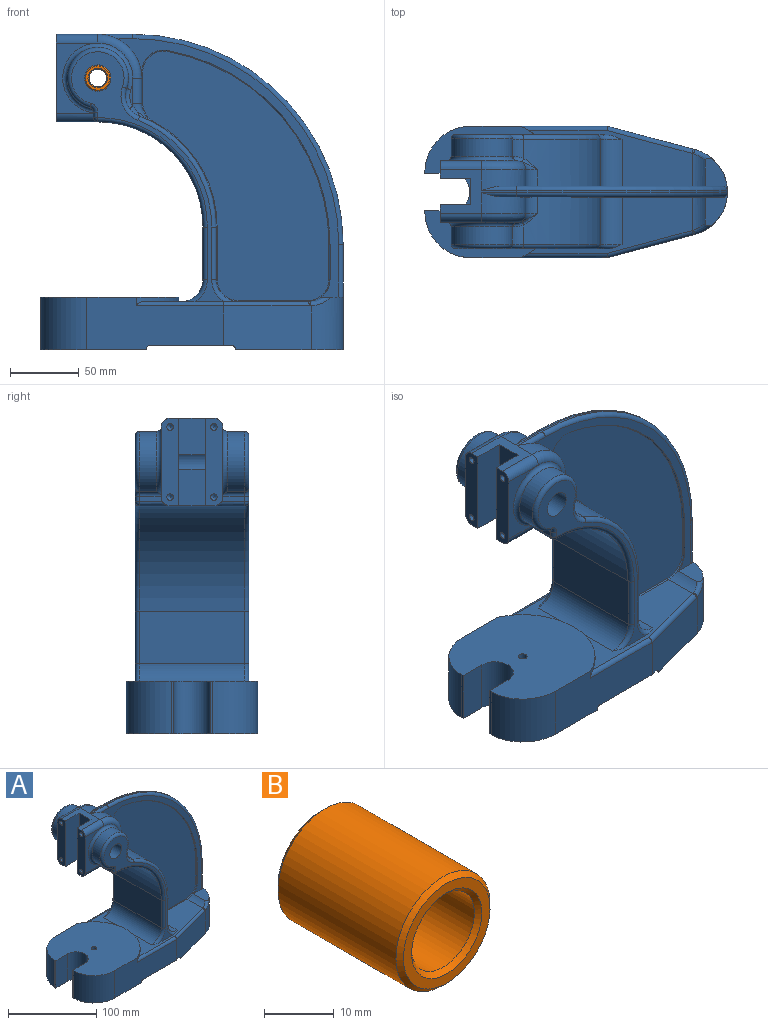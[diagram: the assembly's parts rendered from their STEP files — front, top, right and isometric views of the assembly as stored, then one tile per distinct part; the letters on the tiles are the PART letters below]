
ASSEMBLY  parts=2 mates=1
PART A: 180 faces, bbox 234.5x98.1x244 mm
  f0: plane 63.5x12.7mm, normal (-1,0,0), area 753.5mm2, adj f2,f15,f17,f92,f97,f149,f151,f158
  f1: plane 20.23x2.34mm, normal (0,1,0), area 23.9mm2, adj f90,f91,f104,f106
  f2: plane 50.8x30.1mm, normal (0,-1,0), area 515.4mm2, adj f0,f83,f92,f97,f124
  f3: plane 22.59x12.73mm, normal (1,0,0), area 235.4mm2, adj f19,f26,f32,f87,f94,f174
  f4: plane 22.59x12.73mm, normal (1,0,0), area 235.4mm2, adj f10,f14,f33,f86,f90,f164
  f5: plane 99.19x38.1mm, normal (0,-1,0), area 3202mm2, adj f6,f40,f46,f49,f52,f58,f76,f133
  f6: plane 100x95.25mm, normal (0,0,1), area 7398mm2, adj f5,f43,f44,f48,f54,f55,f56,f57
  f7: plane 38.1x34.96mm, normal (1,0,0), area 1331.9mm2, adj f8,f9,f114,f169
  f8: cylinder r=15.88mm len=34.96mm, axis (0,1,0), area 871.7mm2, adj f7,f37,f115,f167
  f9: cylinder r=85.72mm len=80.21mm, axis (0,1,0), area 3442.3mm2, adj f7,f80,f86,f100,f113,f168
  f10: cylinder r=15.88mm len=18.65mm, axis (0,1,0), area 22.7mm2, adj f4,f11,f33,f162
  f11: cylinder r=142.88mm len=140.67mm, axis (0,1,0), area 163.3mm2, adj f10,f12,f33,f160
  f12: plane 25.4x0.82mm, normal (-1,0,0), area 20.8mm2, adj f11,f13,f33,f161
  f13: cylinder r=15.88mm len=24.81mm, axis (0,1,0), area 242.1mm2, adj f12,f33,f37,f45,f139,f140,f163
  f14: cylinder r=31.75mm len=31.75mm, axis (0,1,0), area 616.8mm2, adj f4,f15,f33,f89,f141
  f15: plane 55.5x31.75mm, normal (0,0,1), area 573.2mm2, adj f0,f14,f16,f19,f31,f88,f92,f141
  f16: plane 63.5x12.7mm, normal (-1,0,0), area 753.5mm2, adj f15,f17,f21,f88,f96,f147,f153,f157
  f17: plane 31.75x30.1mm, normal (0,0,-1), area 533.2mm2, adj f0,f16,f18,f96,f97,f156,f157,f158
  f18: cylinder r=76.2mm len=76.2mm, axis (0,1,0), area 9120.7mm2, adj f17,f22,f103,f105,f119,f121
  f19: cylinder r=31.75mm len=31.75mm, axis (0,1,0), area 616.8mm2, adj f3,f15,f32,f93,f144
  f20: plane 20.23x2.34mm, normal (0,-1,0), area 23.9mm2, adj f94,f95,f122,f124
  f21: plane 50.8x30.1mm, normal (0,1,0), area 515.4mm2, adj f16,f78,f88,f96,f106
  f22: plane 76.2x38.1mm, normal (-1,0,0), area 2903.2mm2, adj f18,f98,f101,f117
  f23: cylinder r=15.88mm len=34.96mm, axis (0,1,0), area 871.7mm2, adj f24,f37,f132,f177
  f24: plane 38.1x34.96mm, normal (1,0,0), area 1331.9mm2, adj f23,f25,f131,f179
  f25: cylinder r=85.72mm len=80.21mm, axis (0,1,0), area 3442.3mm2, adj f24,f81,f87,f118,f130,f178
  f26: cylinder r=15.88mm len=18.65mm, axis (0,1,0), area 22.7mm2, adj f3,f27,f32,f172
  f27: cylinder r=142.88mm len=140.67mm, axis (0,1,0), area 163.3mm2, adj f26,f28,f32,f170
  f28: plane 25.4x0.82mm, normal (-1,0,0), area 20.8mm2, adj f27,f29,f32,f171
  f29: cylinder r=15.88mm len=24.81mm, axis (0,1,0), area 242.1mm2, adj f28,f32,f36,f37,f135,f136,f173
  f30: plane 76.2x7.92mm, normal (1,0,0), area 361.9mm2, adj f31,f36,f42,f45,f51,f53,f143,f146
  f31: cylinder r=152.4mm len=152.4mm, axis (0,1,0), area 377mm2, adj f15,f30,f142,f145
  f32: plane 187.33x160.79mm, normal (0,-1,0), area 1900.4mm2, adj f3,f19,f26,f27,f28,f29,f36,f144
  f33: plane 187.33x160.79mm, normal (0,1,0), area 1900.4mm2, adj f4,f10,f11,f12,f13,f14,f45,f141
  f34: plane 180.67x135mm, normal (0,-1,0), area 14138.8mm2, adj f170,f171,f172,f173,f174,f175,f176,f177
  f35: plane 180.67x135mm, normal (0,1,0), area 14138.8mm2, adj f160,f161,f162,f163,f164,f165,f166,f167
  f36: plane 26.58x18.73mm, normal (0,0,1), area 245.8mm2, adj f29,f30,f32,f53,f136,f146
  f37: plane 119.12x89.67mm, normal (0,0,1), area 4280.2mm2, adj f8,f13,f23,f29,f76,f77,f84,f98
  f38: cylinder r=3.17mm len=9.06mm, axis (0,1,0), area 40.9mm2, adj f40,f42,f52,f69
  f39: cylinder r=3.17mm len=7.93mm, axis (0,1,0), area 39.5mm2, adj f41,f46,f48,f65
  f40: plane 58.73x9.7mm, normal (0,0,-1), area 467.1mm2, adj f5,f38,f49,f52,f64,f69
  f41: plane 58.73x9.7mm, normal (0,0,-1), area 467.1mm2, adj f39,f47,f48,f50,f65,f67
  f42: plane 90.55x77.8mm, normal (0,0,-1), area 1454mm2, adj f30,f38,f47,f50,f51,f52,f53,f59
  f43: plane 38.1x1.61mm, normal (-1,0,0), area 61.5mm2, adj f6,f46,f54,f58
  f44: plane 38.1x1.61mm, normal (-1,0,0), area 61.5mm2, adj f6,f46,f55,f57
  f45: plane 26.58x18.73mm, normal (0,0,1), area 245.8mm2, adj f13,f30,f33,f51,f140,f143
  f46: plane 95.25x76.2mm, normal (0,0,-1), area 2029.8mm2, adj f5,f39,f43,f44,f48,f49,f54,f55
  f47: cylinder r=3.17mm len=9.06mm, axis (0,1,0), area 40.9mm2, adj f41,f42,f50,f67
  f48: plane 99.19x38.1mm, normal (0,1,0), area 3202mm2, adj f6,f39,f41,f46,f50,f57,f76,f137
  f49: cylinder r=3.17mm len=7.93mm, axis (0,1,0), area 39.5mm2, adj f5,f40,f46,f64
  f50: plane 63.64x32.15mm, normal (0.26,0.97,0), area 2053.6mm2, adj f41,f42,f47,f48,f51,f138,f139
  f51: cylinder r=31.75mm len=38.1mm, axis (0,0,-1), area 1379.2mm2, adj f30,f42,f45,f50,f140
  f52: plane 63.64x32.15mm, normal (0.26,-0.97,0), area 2053.6mm2, adj f5,f38,f40,f42,f53,f134,f135
  f53: cylinder r=31.75mm len=38.1mm, axis (0,0,-1), area 1379.2mm2, adj f30,f36,f42,f52,f136
  f54: plane 38.1x19.05mm, normal (0,1,0), area 725.8mm2, adj f6,f43,f46,f56
  f55: plane 38.1x19.05mm, normal (0,-1,0), area 725.8mm2, adj f6,f44,f46,f56
  f56: cylinder r=13.49mm len=38.1mm, axis (0,0,-1), area 1615.1mm2, adj f6,f46,f54,f55
  f57: cylinder r=33.32mm len=38.1mm, axis (0,0,-1), area 1963.7mm2, adj f6,f44,f46,f48
  f58: cylinder r=33.32mm len=38.1mm, axis (0,0,-1), area 1963.7mm2, adj f5,f6,f43,f46
  f59: plane 30.18x6.86mm, normal (-1,0,0), area 207mm2, adj f42,f60,f68,f70
  f60: plane 31.27x5.6mm, normal (0,0,-1), area 124.1mm2, adj f59,f61,f68,f70
  f61: cylinder r=23.8mm len=46.06mm, axis (0,1,0), area 499.2mm2, adj f60,f62,f67,f68,f69,f70
  f62: plane 84.13x79.4mm, normal (0,0,-1), area 5642.5mm2, adj f61,f64,f65,f66,f67,f69
  f63: plane 100.62x79.4mm, normal (0,0,-1), area 6568.5mm2, adj f64,f65,f66,f71,f72,f73,f74,f75
  f64: plane 98.15x30.18mm, normal (0,1,0), area 2718.8mm2, adj f40,f46,f49,f62,f63,f66,f69,f75
  f65: plane 98.15x30.18mm, normal (0,-1,0), area 2718.8mm2, adj f39,f41,f46,f62,f63,f66,f67,f74
  f66: plane 79.4x3.18mm, normal (-1,0,0), area 252.1mm2, adj f62,f63,f64,f65
  f67: plane 62.63x27.36mm, normal (-0.26,-0.97,0), area 1710.8mm2, adj f41,f42,f47,f61,f62,f65,f68
  f68: cylinder r=23.83mm len=30.18mm, axis (0,0,-1), area 814.8mm2, adj f42,f59,f60,f61,f67
  f69: plane 62.63x27.36mm, normal (-0.26,0.97,0), area 1710.8mm2, adj f38,f40,f42,f61,f62,f64,f70
  f70: cylinder r=23.83mm len=30.18mm, axis (0,0,-1), area 814.8mm2, adj f42,f59,f60,f61,f69
  f71: plane 30.18x10.12mm, normal (0,-1,0), area 305.3mm2, adj f46,f63,f73,f75
  f72: plane 30.18x10.12mm, normal (0,1,0), area 305.3mm2, adj f46,f63,f73,f74
  f73: cylinder r=21.42mm len=42.84mm, axis (0,0,-1), area 2030.4mm2, adj f46,f63,f71,f72
  f74: cylinder r=25.4mm len=30.18mm, axis (0,0,-1), area 986.2mm2, adj f46,f63,f65,f72
  f75: cylinder r=25.4mm len=30.18mm, axis (0,0,-1), area 986.2mm2, adj f46,f63,f64,f71
  f76: cylinder r=52.37mm len=95.25mm, axis (0,0,1), area 401mm2, adj f5,f6,f37,f48,f133,f137
  f77: plane 180.98x110.12mm, normal (0,1,0), area 1717.8mm2, adj f37,f85,f99,f101,f103,f109,f110,f111
  f78: plane 16.73x3.98mm, normal (-1,0,0), area 64.1mm2, adj f21,f96,f105,f106,f108,f109
  f79: cylinder r=22.23mm len=44.45mm, axis (0,1,0), area 1356.2mm2, adj f80,f106,f108,f111
  f80: cylinder r=15.88mm len=20.22mm, axis (0,1,0), area 319.4mm2, adj f9,f79,f102,f104,f112
  f81: cylinder r=15.88mm len=20.22mm, axis (0,1,0), area 319.4mm2, adj f25,f82,f120,f122,f129
  f82: cylinder r=22.23mm len=44.45mm, axis (0,1,0), area 1356.2mm2, adj f81,f124,f126,f128
  f83: plane 16.73x3.98mm, normal (-1,0,0), area 64.1mm2, adj f2,f97,f121,f124,f125,f126
  f84: plane 180.98x110.12mm, normal (0,-1,0), area 1717.8mm2, adj f37,f85,f116,f117,f119,f125,f127,f128
  f85: cylinder r=9.53mm len=82.55mm, axis (0,1,0), area 4727mm2, adj f77,f84,f156,f157,f158,f159
  f86: cylinder r=15.88mm len=14.02mm, axis (0,1,0), area 218.9mm2, adj f4,f9,f91,f166
  f87: cylinder r=15.88mm len=14.02mm, axis (0,1,0), area 218.9mm2, adj f3,f25,f95,f176
  f88: cylinder r=6.35mm len=30.1mm, axis (-1,0,0), area 300.2mm2, adj f15,f16,f21,f89
  f89: torus R=25.4mm, axis (0,-1,0), area 461.3mm2, adj f14,f88,f90,f106
  f90: cylinder r=6.35mm len=18.2mm, axis (0,0,1), area 181.6mm2, adj f1,f4,f89,f91
  f91: torus R=22.23mm, axis (0,-1,0), area 98mm2, adj f1,f86,f90,f100,f102
  f92: cylinder r=6.35mm len=30.1mm, axis (1,0,0), area 300.2mm2, adj f0,f2,f15,f93
  f93: torus R=25.4mm, axis (0,-1,0), area 461.3mm2, adj f19,f92,f94,f124
  f94: cylinder r=6.35mm len=18.2mm, axis (0,0,-1), area 181.6mm2, adj f3,f20,f93,f95
  f95: torus R=22.23mm, axis (0,-1,0), area 98mm2, adj f20,f87,f94,f118,f120
  f96: cylinder r=6.35mm len=30.1mm, axis (1,0,0), area 279.1mm2, adj f16,f17,f21,f78,f105
  f97: cylinder r=6.35mm len=30.1mm, axis (-1,0,0), area 279.1mm2, adj f0,f2,f17,f83,f121
  f98: cylinder r=15.88mm len=76.2mm, axis (0,-1,0), area 1900.2mm2, adj f22,f37,f99,f116
  f99: torus R=19.05mm, axis (0,-1,0), area 107.7mm2, adj f37,f77,f98,f101
  f100: bspline ~12.01x8.85mm, area 17.9mm2, adj f9,f91,f102
  f101: cylinder r=3.17mm len=38.1mm, axis (0,0,-1), area 190mm2, adj f22,f77,f99,f103
  f102: bspline ~10.6x9.56mm, area 36.6mm2, adj f80,f91,f100,f104
  f103: torus R=79.38mm, axis (0,-1,0), area 606mm2, adj f18,f77,f101,f107
  f104: torus R=12.7mm, axis (0,-1,0), area 70.6mm2, adj f1,f80,f102,f106
  f105: cylinder r=3.17mm len=22.23mm, axis (0,1,0), area 97.1mm2, adj f18,f78,f96,f107
  f106: torus R=25.4mm, axis (0,-1,0), area 570mm2, adj f1,f21,f78,f79,f89,f104,f108
  f107: sphere r=3.17mm, area 21.6mm2, adj f103,f105,f109
  f108: cylinder r=3.17mm len=15.82mm, axis (0,1,0), area 59.7mm2, adj f78,f79,f106,f110
  f109: cylinder r=3.17mm len=3.98mm, axis (0,0,-1), area 19.9mm2, adj f77,f78,f107,f110
  f110: torus R=6.35mm, axis (0,-1,0), area 28.5mm2, adj f77,f108,f109,f111
  f111: torus R=19.05mm, axis (0,-1,0), area 504.9mm2, adj f77,f79,f110,f112
  f112: torus R=19.05mm, axis (0,-1,0), area 132.1mm2, adj f77,f80,f111,f113
  f113: torus R=82.55mm, axis (0,-1,0), area 510.4mm2, adj f9,f77,f112,f114
  f114: cylinder r=3.17mm len=38.1mm, axis (0,0,1), area 190mm2, adj f7,f77,f113,f115
  f115: torus R=19.05mm, axis (0,-1,0), area 107.7mm2, adj f8,f37,f77,f114
  f116: torus R=19.05mm, axis (0,-1,0), area 107.7mm2, adj f37,f84,f98,f117
  f117: cylinder r=3.17mm len=38.1mm, axis (0,0,1), area 190mm2, adj f22,f84,f116,f119
  f118: bspline ~11.06x8.44mm, area 17.9mm2, adj f25,f95,f120
  f119: torus R=79.38mm, axis (0,-1,0), area 606mm2, adj f18,f84,f117,f123
  f120: bspline ~9.12x8.99mm, area 36.6mm2, adj f81,f95,f118,f122
  f121: cylinder r=3.17mm len=22.23mm, axis (0,1,0), area 97.1mm2, adj f18,f83,f97,f123
  f122: torus R=12.7mm, axis (0,-1,0), area 70.6mm2, adj f20,f81,f120,f124
  f123: sphere r=3.17mm, area 15.8mm2, adj f119,f121,f125
  f124: torus R=25.4mm, axis (0,-1,0), area 570mm2, adj f2,f20,f82,f83,f93,f122,f126
  f125: cylinder r=3.17mm len=3.98mm, axis (0,0,1), area 19.9mm2, adj f83,f84,f123,f127
  f126: cylinder r=3.17mm len=15.82mm, axis (0,1,0), area 59.7mm2, adj f82,f83,f124,f127
  f127: torus R=6.35mm, axis (0,-1,0), area 28.5mm2, adj f84,f125,f126,f128
  f128: torus R=19.05mm, axis (0,-1,0), area 504.9mm2, adj f82,f84,f127,f129
  f129: torus R=19.05mm, axis (0,-1,0), area 132.1mm2, adj f81,f84,f128,f130
  f130: torus R=82.55mm, axis (0,-1,0), area 510.4mm2, adj f25,f84,f129,f131
  f131: cylinder r=3.17mm len=38.1mm, axis (0,0,-1), area 190mm2, adj f24,f84,f130,f132
  f132: torus R=19.05mm, axis (0,-1,0), area 107.7mm2, adj f23,f37,f84,f131
  f133: cylinder r=3.17mm len=63.09mm, axis (1,0,0), area 298.9mm2, adj f5,f37,f76,f134
  f134: cylinder r=3.17mm len=62.81mm, axis (0.97,0.26,0), area 319mm2, adj f37,f52,f133,f135
  f135: bspline ~3.41x3.21mm, area 6mm2, adj f29,f52,f134,f136
  f136: bspline ~18.95x11.92mm, area 79.7mm2, adj f29,f36,f53,f135
  f137: cylinder r=3.17mm len=63.09mm, axis (-1,0,0), area 298.9mm2, adj f37,f48,f76,f138
  f138: cylinder r=3.17mm len=62.81mm, axis (-0.97,0.26,0), area 319mm2, adj f37,f50,f137,f139
  f139: bspline ~6.89x4.84mm, area 6mm2, adj f13,f50,f138,f140
  f140: bspline ~17.46x11.57mm, area 79.7mm2, adj f13,f45,f51,f139
  f141: cylinder r=3.17mm len=25.4mm, axis (-1,0,0), area 92.2mm2, adj f14,f15,f33,f142
  f142: torus R=149.22mm, axis (0,-1,0), area 1184.9mm2, adj f31,f33,f141,f143
  f143: cylinder r=3.17mm len=38.1mm, axis (0,0,1), area 190mm2, adj f30,f33,f45,f142
  f144: cylinder r=3.17mm len=25.4mm, axis (1,0,0), area 92.2mm2, adj f15,f19,f32,f145
  f145: torus R=149.22mm, axis (0,-1,0), area 1184.9mm2, adj f31,f32,f144,f146
  f146: cylinder r=3.17mm len=38.1mm, axis (0,0,-1), area 190mm2, adj f30,f32,f36,f145
  f147: cylinder r=2.38mm len=6.35mm, axis (-1,0,0), area 95mm2, adj f16,f148
  f148: cone r=0mm half-angle=59deg, axis (-1,0,0), area 20.8mm2, adj f147
  f149: cylinder r=2.38mm len=6.35mm, axis (-1,0,0), area 95mm2, adj f0,f150
  f150: cone r=0mm half-angle=59deg, axis (-1,0,0), area 20.8mm2, adj f149
  f151: cylinder r=2.38mm len=6.35mm, axis (-1,0,0), area 95mm2, adj f0,f152
  f152: cone r=0mm half-angle=59deg, axis (-1,0,0), area 20.8mm2, adj f151
  f153: cylinder r=2.38mm len=6.35mm, axis (-1,0,0), area 95mm2, adj f16,f154
  f154: cone r=0mm half-angle=59deg, axis (-1,0,0), area 20.8mm2, adj f153
  f155: cylinder r=3.17mm len=7.93mm, axis (0,0,1), area 158.1mm2, adj f6,f63
  f156: plane 26.47x19.05mm, normal (-1,0,0), area 504.2mm2, adj f17,f85,f157,f158
  f157: plane 63.5x22.17mm, normal (0,-1,0), area 1396.6mm2, adj f15,f16,f17,f85,f156,f159
  f158: plane 63.5x22.17mm, normal (0,1,0), area 1396.6mm2, adj f0,f15,f17,f85,f156,f159
  f159: plane 26.47x19.05mm, normal (-1,0,0), area 504.2mm2, adj f15,f85,f157,f158
  f160: torus R=142.11mm, axis (0,-1,0), area 238.1mm2, adj f11,f35,f161,f162
  f161: cylinder r=0.76mm len=25.4mm, axis (0,0,1), area 30.4mm2, adj f12,f35,f160,f163
  f162: torus R=15.11mm, axis (0,-1,0), area 32.6mm2, adj f10,f35,f160,f164
  f163: torus R=15.11mm, axis (0,-1,0), area 29.3mm2, adj f13,f35,f161,f165
  f164: cylinder r=0.76mm len=22.59mm, axis (0,0,1), area 27mm2, adj f4,f35,f162,f166
  f165: cylinder r=0.76mm len=50.8mm, axis (1,0,0), area 60.8mm2, adj f35,f37,f163,f167
  f166: torus R=15.11mm, axis (0,-1,0), area 20.2mm2, adj f35,f86,f164,f168
  f167: torus R=15.11mm, axis (0,-1,0), area 29.3mm2, adj f8,f35,f165,f169
  f168: torus R=86.49mm, axis (0,-1,0), area 111.5mm2, adj f9,f35,f166,f169
  f169: cylinder r=0.76mm len=38.1mm, axis (0,0,-1), area 45.6mm2, adj f7,f35,f167,f168
  f170: torus R=142.11mm, axis (0,-1,0), area 238.1mm2, adj f27,f34,f171,f172
  f171: cylinder r=0.76mm len=25.4mm, axis (0,0,-1), area 30.4mm2, adj f28,f34,f170,f173
  f172: torus R=15.11mm, axis (0,-1,0), area 32.6mm2, adj f26,f34,f170,f174
  f173: torus R=15.11mm, axis (0,-1,0), area 29.3mm2, adj f29,f34,f171,f175
  f174: cylinder r=0.76mm len=22.59mm, axis (0,0,-1), area 27mm2, adj f3,f34,f172,f176
  f175: cylinder r=0.76mm len=50.8mm, axis (-1,0,0), area 60.8mm2, adj f34,f37,f173,f177
  f176: torus R=15.11mm, axis (0,-1,0), area 20.2mm2, adj f34,f87,f174,f178
  f177: torus R=15.11mm, axis (0,-1,0), area 29.3mm2, adj f23,f34,f175,f179
  f178: torus R=86.49mm, axis (0,-1,0), area 111.5mm2, adj f25,f34,f176,f179
  f179: cylinder r=0.76mm len=38.1mm, axis (0,0,1), area 45.6mm2, adj f24,f34,f177,f178
PART B: 8 faces, bbox 19.1x25.4x19.1 mm
  f0: plane 17.53x17.53mm, normal (0,-1,0), area 82.3mm2, adj f4,f5
  f1: plane 17.53x17.53mm, normal (0,1,0), area 82.3mm2, adj f6,f7
  f2: cylinder r=9.53mm len=23.88mm, axis (0,1,0), area 1428.9mm2, adj f4,f7
  f3: cylinder r=6.35mm len=23.88mm, axis (0,1,0), area 952.6mm2, adj f5,f6
  f4: cone r=9.53mm half-angle=45deg, axis (0,1,0), area 61.9mm2, adj f0,f2
  f5: cone r=6.35mm half-angle=45deg, axis (0,-1,0), area 45.6mm2, adj f0,f3
  f6: cone r=6.35mm half-angle=45deg, axis (0,1,0), area 45.6mm2, adj f1,f3
  f7: cone r=9.53mm half-angle=45deg, axis (0,-1,0), area 61.9mm2, adj f1,f2
PLACE A t=(-4.35,5.05,0.95)mm fixed
PLACE B t=(-4.35,5.05,0.95)mm
MATE fastened B.f2 <-> A.f14  axis (0,1,0) through (-4.35,46.33,0.95)mm
